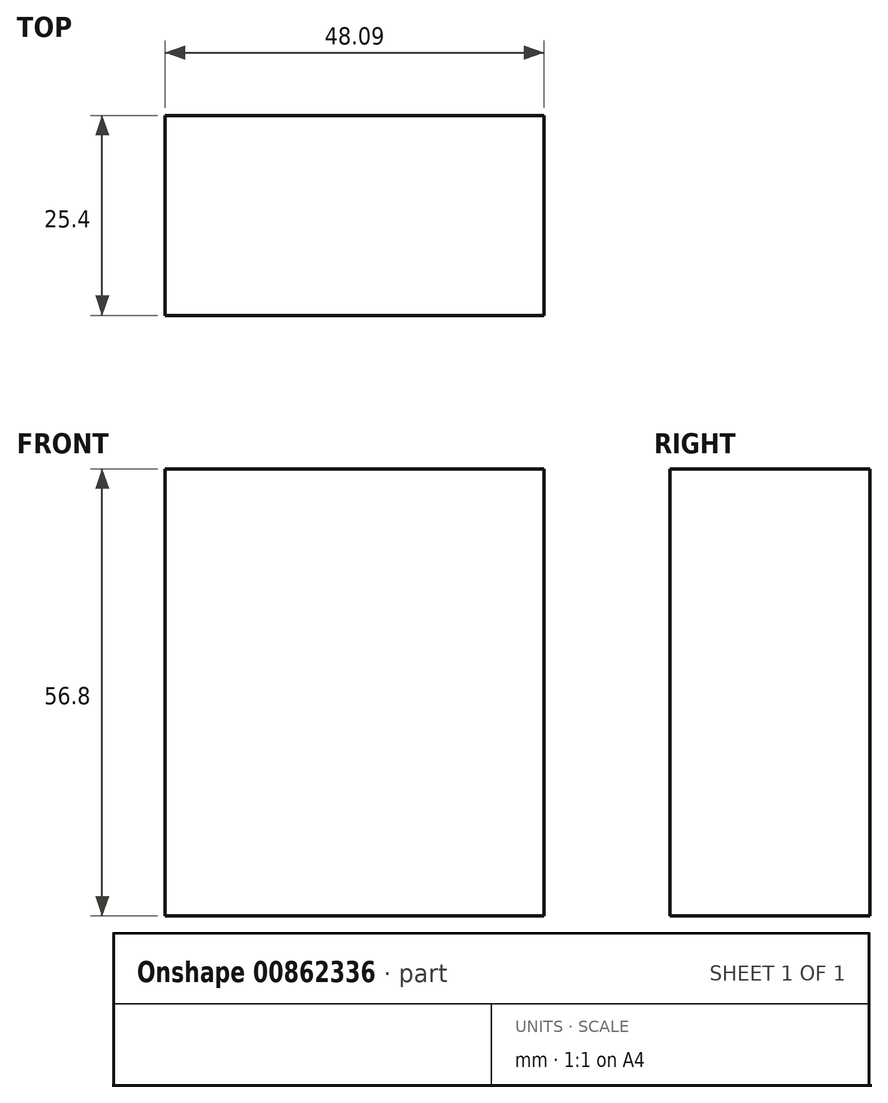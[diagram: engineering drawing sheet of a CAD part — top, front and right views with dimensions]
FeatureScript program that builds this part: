
annotation { "Feature Type Name" : "Feature", "Feature Type Description" : "" }
export const myFeature = defineFeature(function(context is Context, id is Id, definition is map)
    precondition{}
    {
        {
            var Q0;
            Q0=qCreatedBy(makeId("Front.planeOp"),FACE);
            var sketch = newSketch(context, id + "F0", { "sketchPlane" : qUnion([Q0])});
            skLineSegment(sketch, "E0.bottom", {"start": v(-94.44, 38.35) * mm, "end": v(-46.35, 38.35) * mm});
            skLineSegment(sketch, "E0.top", {"start": v(-94.44, -18.45) * mm, "end": v(-46.35, -18.45) * mm});
            skLineSegment(sketch, "E0.left", {"start": v(-94.44, 38.35) * mm, "end": v(-94.44, -18.45) * mm});
            skLineSegment(sketch, "E0.right", {"start": v(-46.35, 38.35) * mm, "end": v(-46.35, -18.45) * mm});
            skSolve(sketch);
        }
        {
            var Q0;
            Q0 = qSketchRegion(id + "F0", true);
            extrude(context, id + "F1", {"entities" : qUnion([Q0]), "depth" : 25.4 * mm, "offsetDistance" : 25.4 * mm});
        }
    });
